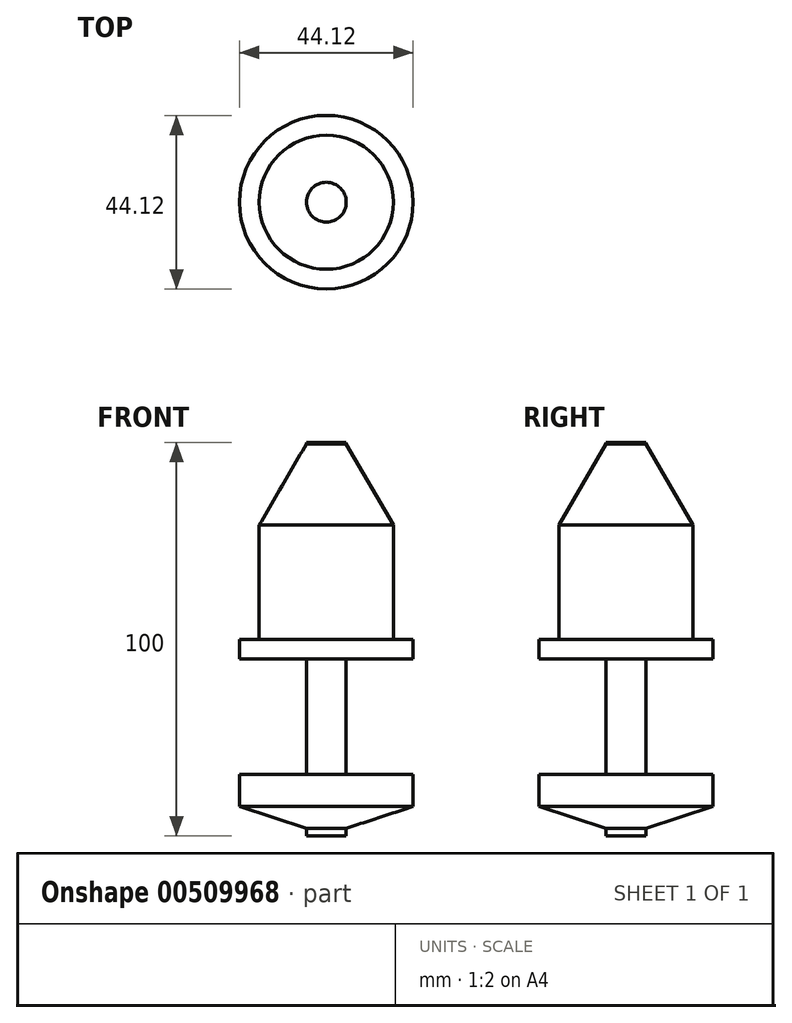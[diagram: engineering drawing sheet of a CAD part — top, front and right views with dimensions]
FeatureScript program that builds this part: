
annotation { "Feature Type Name" : "Feature", "Feature Type Description" : "" }
export const myFeature = defineFeature(function(context is Context, id is Id, definition is map)
    precondition{}
    {
        {
            var Q0;
            Q0=qCreatedBy(makeId("Top.planeOp"),FACE);
            var sketch = newSketch(context, id + "F0", { "sketchPlane" : qUnion([Q0])});
            skCircle(sketch, "E0", {"center": v(0, 0) * mm, "radius": 5.06 * mm});
            skSolve(sketch);
        }
        {
            var Q0;
            Q0 = qSketchRegion(id + "F0", true);
            extrude(context, id + "F1", {"entities" : qUnion([Q0]), "endBound" : BoundingType.SYMMETRIC, "depth" : 100 * mm});
        }
        {
            var Q0;
            Q0=qCreatedBy(makeId("Right.planeOp"),FACE);
            var sketch = newSketch(context, id + "F2", { "sketchPlane" : qUnion([Q0])});
            skLineSegment(sketch, "E1", {"start": v(0, 49.7) * mm, "end": v(5.03, 49.7) * mm});
            skLineSegment(sketch, "E2", {"start": v(5.03, 49.7) * mm, "end": v(17.03, 29.04) * mm});
            skLineSegment(sketch, "E3", {"start": v(17.03, 29.04) * mm, "end": v(17.03, 0) * mm});
            skLineSegment(sketch, "E4", {"start": v(17.03, 0) * mm, "end": v(22.06, 0) * mm});
            skLineSegment(sketch, "E5", {"start": v(22.06, 0) * mm, "end": v(22.06, -5.03) * mm});
            skLineSegment(sketch, "E6", {"start": v(22.06, -5.03) * mm, "end": v(0, -5.03) * mm});
            skLineSegment(sketch, "E7", {"start": v(0, -5.03) * mm, "end": v(0, -34.35) * mm});
            skLineSegment(sketch, "E8", {"start": v(0, -34.35) * mm, "end": v(22.06, -34.35) * mm});
            skLineSegment(sketch, "E9", {"start": v(22.06, -34.35) * mm, "end": v(22.06, -42.45) * mm});
            skLineSegment(sketch, "E10", {"start": v(22.06, -42.45) * mm, "end": v(0, -49.7) * mm});
            skLineSegment(sketch, "E11", {"start": v(0, -49.7) * mm, "end": v(0, -34.35) * mm});
            skLineSegment(sketch, "E12", {"start": v(0, 49.7) * mm, "end": v(0, -9.77) * mm});
            skSolve(sketch);
        }
        {
            var Q0;
            {var subQ0=sQuery(id+"F2.wireOp",EDGE,"E1");Q0=makeQuery(id+"F2.imprint","IMPRINT",FACE,{"disambiguationData":[TD([[makeQuery(id+"F2.imprint","IMPRINT",EDGE,{"derivedFrom":subQ0}),-1.0]])]});}
            var Q1;
            Q1=makeQuery(id+"F2.imprint","IMPRINT",FACE,{"disambiguationData":[TD([[makeQuery(id+"F2.imprint","IMPRINT",EDGE,{"derivedFrom":sQuery(id+"F2.wireOp",EDGE,"E8")}),-1.0]])]});
            var Q2;
            Q2=sQuery(id+"F2.wireOp",EDGE,"E12");
            revolve(context, id + "F3", {"operationType" : NewBodyOperationType.ADD, "entities" : qUnion([Q0, Q1]), "axis" : qUnion([Q2]), "revolveType" : RevolveType.FULL});
        }
    });
